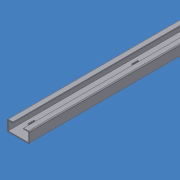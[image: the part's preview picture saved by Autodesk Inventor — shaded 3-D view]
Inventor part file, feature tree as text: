
AUTODESK INVENTOR PART (.ipt)
format: ipt  version: 2015 SP1 (Build 190203100, 203)  size: 250,368 bytes
history: native  units: mm
features: sheet_metal_op x9, other x8, sketch x6, plane x2
ambient origin geometry x8: Origin, YZ Plane, XZ Plane, XY Plane, X Axis, Y Axis, Z Axis, Center Point
bodies: Solid1 (feature_tree)
feature tree (25):
  sheet_metal_op  "Face1"
  sheet_metal_op  "Flange1"
  sheet_metal_op  "Flange2"
  sheet_metal_op  "Flange3"
  sheet_metal_op  "Flange4"
  plane  "Work Plane4"
  plane  "Work Plane6"
  sketch  "Sketch1"  dims[d4=0.001mm]
  other  "Plate1"
  sketch  "Sketch2"  dims[d5=3.0mm]
  other  "Plate2"
  sheet_metal_op  "Bend1"
  sketch  "Sketch3"  dims[d6=0.001mm]
  other  "Plate3"
  sheet_metal_op  "Bend2"
  sketch  "Sketch4"  dims[d7=6.0mm]
  other  "Plate4"
  sheet_metal_op  "Bend3"
  sketch  "Sketch5"  dims[d8=0.001mm]
  other  "Plate5"
  sheet_metal_op  "Bend4"
  sketch  "Sketch6"  dims[d9=29.0mm d10=90.0deg d11=0.001mm d12=3.0mm d13=0.001mm d14=6.0mm d15=0.001mm d16=29.0mm d17=90.0deg d18=0.001mm d19=3.0mm d20=0.001mm d21=6.0mm d22=0.001mm d23=15.0mm d24=90.0deg d25=0.001mm d26=3.0mm d27=0.001mm d28=6.0mm d29=0.001mm d30=15.0mm d31=90.0deg d32=0.001mm d33=4.0mm d34=20.5mm d35=4.0mm d36=20.5mm d37=0.0mm d38=33.0mm d40=4.0mm d41=0.0mm d42=550.0mm d45=150.0mm d46=10.0mm d47=10.0mm d48=64.0mm d49=6.0mm d50=64.0mm d51=4.0mm d52=9.0mm d62=20.5mm d63=4.0mm d64=9.0mm d65=20.5mm d66=4.0mm d68=4.0mm d69=0.0mm d71=50.0mm d72=33.0mm d73=16.5mm d0=3.0mm]
  other  "FlatPattern"
  other  "Cut1"
  other  "FlatPatternExtrusion2"
